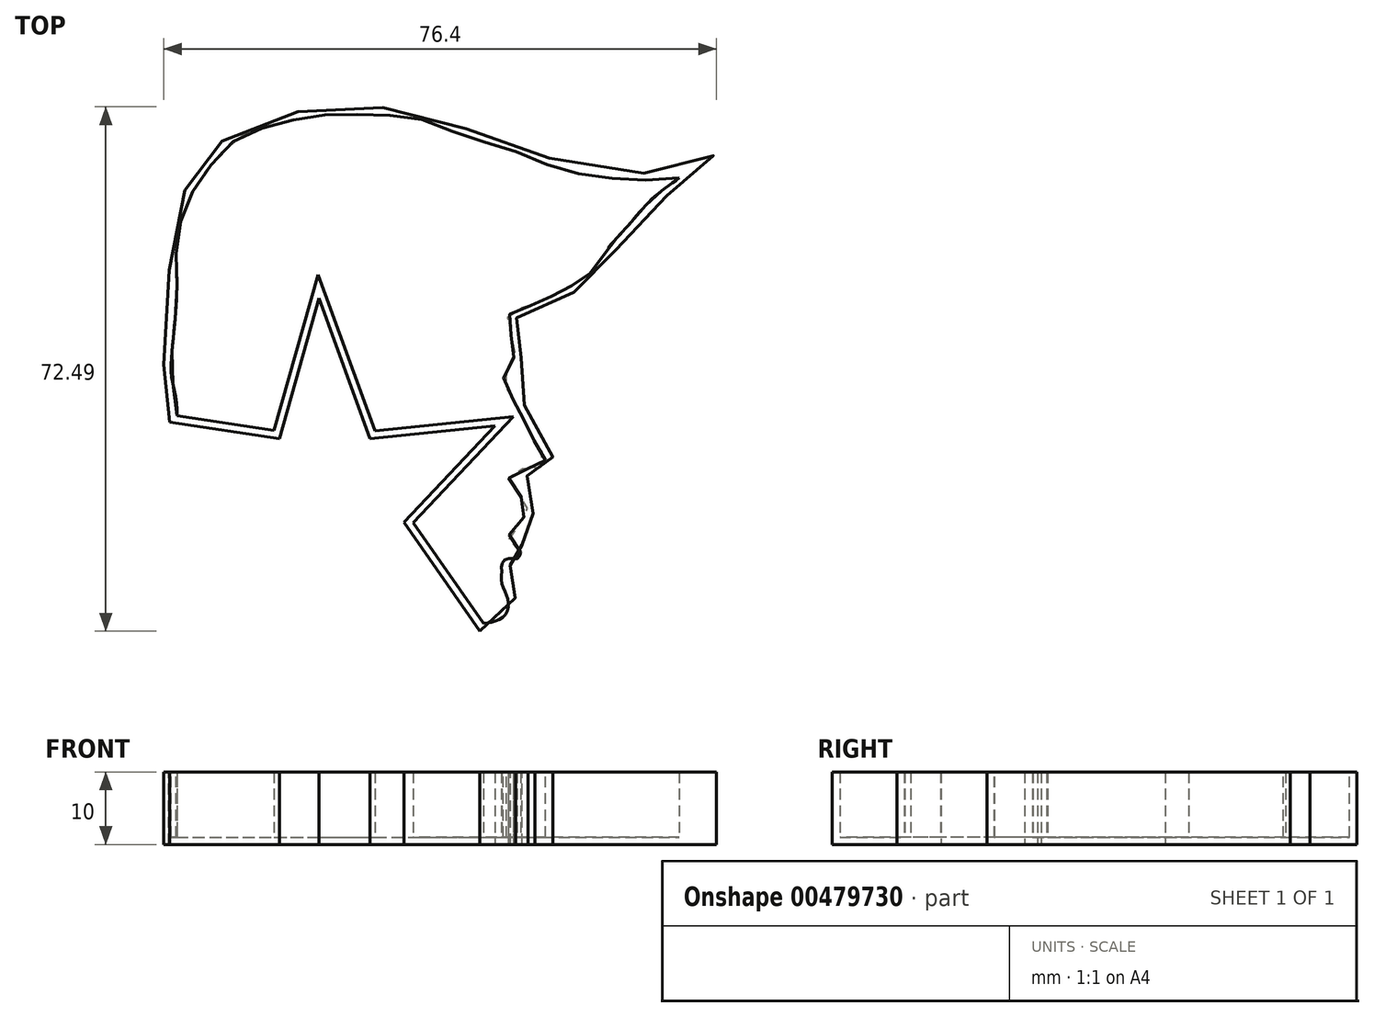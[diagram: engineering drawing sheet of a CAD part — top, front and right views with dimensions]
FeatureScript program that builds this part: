
annotation { "Feature Type Name" : "Feature", "Feature Type Description" : "" }
export const myFeature = defineFeature(function(context is Context, id is Id, definition is map)
    precondition{}
    {
        {
            var Q0;
            Q0=qCreatedBy(makeId("Top.planeOp"),FACE);
            var sketch = newSketch(context, id + "F0", { "sketchPlane" : qUnion([Q0])});
            skLineSegment(sketch, "E0", {"start": v(-29.84, -7.59) * mm, "end": v(-14.67, -9.88) * mm});
            skLineSegment(sketch, "E1", {"start": v(-14.67, -9.88) * mm, "end": v(-9.22, 9.54) * mm});
            skLineSegment(sketch, "E2", {"start": v(-9.22, 9.54) * mm, "end": v(-2.13, -9.88) * mm});
            skLineSegment(sketch, "E3", {"start": v(-2.13, -9.88) * mm, "end": v(15.11, -8.13) * mm});
            skLineSegment(sketch, "E4", {"start": v(15.11, -8.13) * mm, "end": v(2.57, -21.44) * mm});
            skLineSegment(sketch, "E5", {"start": v(2.57, -21.44) * mm, "end": v(13.04, -36.5) * mm});
            skFitSpline(sketch, "E6", {"points": [v(-29.84, -7.59) * mm, v(-29.84, -5.24) * mm, v(-30.56, -1.44) * mm, v(-30.56, 1.66) * mm, v(-29.84, 11.14) * mm, v(-29.84, 17.52) * mm, v(-28.06, 23.72) * mm, v(-25.9, 27.34) * mm, v(-24.22, 29.36) * mm, v(-21.2, 32.37) * mm, v(-15.67, 34.47) * mm, v(-8.47, 35.9) * mm, v(-2.19, 35.9) * mm, v(4.68, 35.4) * mm, v(10.97, 33.04) * mm, v(17.75, 30.95) * mm, v(24.62, 28.27) * mm, v(33.75, 26.93) * mm, v(38.6, 26.93) * mm, v(43.78, 28.25) * mm, v(45.74, 29.55) * mm, v(42.86, 26.67) * mm, v(37.65, 22.67) * mm, v(33.75, 18.3) * mm, v(31.52, 15.8) * mm, v(29.85, 13.2) * mm, v(27.43, 11.15) * mm, v(23.44, 8.92) * mm, v(20.56, 7.62) * mm, v(17.86, 6.6) * mm, v(17.86, 5.67) * mm, v(18.51, 4.37) * mm, v(18.89, 2.51) * mm, v(18.24, 0) * mm, v(17.3, -1.58) * mm, v(18.51, -4) * mm, v(20.37, -7.59) * mm, v(22.23, -10.95) * mm, v(23.1, -12.35) * mm, v(22.9, -13.74) * mm, v(22.36, -14.54) * mm, v(21.3, -14.94) * mm, v(19.97, -15.07) * mm, v(18.05, -15.34) * mm, v(20.37, -18.33) * mm, v(20.5, -19.99) * mm, v(19.44, -22.18) * mm, v(18.18, -23.24) * mm, v(18.05, -23.77) * mm, v(18.64, -24.44) * mm, v(19.57, -25.17) * mm, v(19.44, -26.5) * mm, v(18.58, -27.43) * mm, v(17.78, -27.5) * mm, v(17.05, -27.5) * mm, v(17.05, -27.96) * mm, v(17.05, -28.82) * mm, v(17.12, -29.88) * mm, v(17.71, -31.28) * mm, v(17.83, -34.03) * mm, v(15.97, -35.9) * mm, v(13.04, -36.5) * mm], "startDerivative": vector(11.22, 148.37) * mm, "endDerivative": vector(-186.24, -19) * mm});
            skSolve(sketch);
        }
        {
            var Q0;
            Q0=makeQuery(id+"F0.imprint","IMPRINT",FACE,{"disambiguationData":[TD([[makeQuery(id+"F0.imprint","IMPRINT",EDGE,{"derivedFrom":sQuery(id+"F0.wireOp",EDGE,"E0")}),1.0]])]});
            extrude(context, id + "F1", {"entities" : qUnion([Q0]), "depth" : 10 * mm});
        }
        {
            var Q0;
            Q0=makeQuery(id+"F1.opExtrude","CAP_FACE",FACE,{"disambiguationData":[OSD([sQuery(id+"F0.wireOp",EDGE,"E0"),sQuery(id+"F0.wireOp",EDGE,"E1"),sQuery(id+"F0.wireOp",EDGE,"E2"),sQuery(id+"F0.wireOp",EDGE,"E3"),sQuery(id+"F0.wireOp",EDGE,"E4"),sQuery(id+"F0.wireOp",EDGE,"E5"),sQuery(id+"F0.wireOp",EDGE,"E6")])],"isStart":false});
            shell(context, id + "F2", {"entities" : qUnion([Q0]), "thickness" : 1 * mm});
        }
    });
